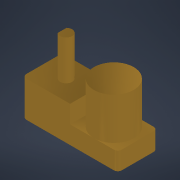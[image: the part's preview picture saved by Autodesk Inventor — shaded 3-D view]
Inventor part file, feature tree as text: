
AUTODESK INVENTOR PART (.ipt)
format: ipt  version: 2022 (Build 260153000, 153)  size: 140,288 bytes
history: native  units: mm
features: extrude x5, sketch x5, projected_geometry x3, fillet x1
ambient origin geometry x8: Origin, YZ Plane, XZ Plane, XY Plane, X Axis, Y Axis, Z Axis, Center Point
bodies: Solid1 (feature_tree)
feature tree (14):
  extrude  "Extrusion1"  Depth=10.0mm TaperAngle=0.0deg
  extrude  "Extrusion2"  Depth=12.0mm
  extrude  "Extrusion3"  Depth=12.0mm TaperAngle=0.0deg
  extrude  "Extrusion4"  Depth=10.5mm TaperAngle=0.0deg
  fillet  "Fillet1"  Radius=1.0mm
  extrude  "Extrusion5"  Depth=9.0mm TaperAngle=0.0deg
  sketch  "Sketch1"  dims[d0=3.0mm d1=10.0mm d2=0.0mm]
  sketch  "Sketch2"  dims[d3=10.0mm d4=12.0mm]
  sketch  "Sketch3"  dims[d5=9.0mm d6=0.0mm d7=12.0mm d8=0.0mm]
  projected_geometry  "Projected Loop1"
  sketch  "Sketch4"  dims[d9=10.0mm d10=10.5mm d11=0.0mm d12=1.0mm]
  projected_geometry  "Projected Loop2"
  sketch  "Sketch5"  dims[d13=0.5mm d14=9.0mm d15=0.0mm]
  projected_geometry  "Projected Loop3"
